FCSTD DOCUMENT  (FreeCAD 0.18.4R)
Label: container.v5
License: All rights reserved
LicenseURL: http://en.wikipedia.org/wiki/All_rights_reserved
objects: Part::Extrusion×24, Part::Feature×12, Part::Part2DObjectPython×12, Part::Cut×11, Part::MultiFuse×11
note: 70 computed .brp shape members not serialized (recipe doc carries the construction recipe); baked Part::Feature solids carry a one-line shape summary decoded from their .brp

FEATURE [Part::Feature] Cut001001  label="Cut002"
  shape: bbox 73.48 x 120 x 121.6 mm, 4537 faces (baked)
FEATURE [Part::Feature] Fusion018002001008015
  shape: bbox 73.48 x 120 x 121.6 mm, 4525 faces (baked)
FEATURE [Part::Feature] Fusion018002001008014
  Placement = pos=(1.059e-12,-240,-121.554) rot=(0,0,1;0rad)
  shape: bbox 46.3 x 120 x 5.151 mm, 1154 faces (baked)
FEATURE [Part::Part2DObjectPython] Rectangle  # Draft 2D object (typed FeaturePython)
  ChamferSize = 0
  Columns = 1
  FilletRadius = 0
  Height = 120
  Length = 112.55
  MakeFace = true
  Placement = pos=(139.139,-112.777,-9.82831) rot=(0,1,0;1.46952rad)
  Rows = 1
FEATURE [Part::Extrusion] Extrusion
  Base = -> Rectangle
  Dir = (9.01598,-9e-16,0.916258)
  DirMode = 0
  FaceMakerClass = Part::FaceMakerBullseye
  LengthFwd = 0
  LengthRev = 0
  Solid = true
  Symmetric = false
FEATURE [Part::Cut] Cut
  Base = -> Fusion018002001008015
  Tool = -> Extrusion
FEATURE [Part::Feature] Face001
  Placement = pos=(20.8688,3.98e-13,-59.6902) rot=(0,0,1;0rad)
  shape: bbox 0.5074 x 117 x 4.974 mm, 1 faces, 0 solids (baked)
FEATURE [Part::Extrusion] Extrusion002
  Base = -> Face001
  Dir = (1.9794,3.87e-14,0.201929)
  DirMode = 0
  FaceMakerClass = Part::FaceMakerBullseye
  LengthFwd = 0
  LengthRev = 0
  Solid = true
  Symmetric = false
FEATURE [Part::Part2DObjectPython] Wire001  # Draft 2D object (typed FeaturePython)
  ChamferSize = 0
  Closed = true
  End = (150.569,7.2227,-121.796)
  FilletRadius = 0
  Length = 3.03695
  MakeFace = true
  Placement = pos=(150.519,7.2227,-121.802) rot=(-1,0,0;1.5708rad)
  Points = (3) [(0,0,0),(0.207003,1.47911,-5.72875e-13),(0.0507037,-0.00515282,-2.84217e-14)]
  Start = (150.519,7.2227,-121.802)
  Subdivisions = 0
FEATURE [Part::Extrusion] Extrusion001
  Base = -> Wire001
  Dir = (-6.89207e-11,-133.783,4.03232e-11)
  DirMode = 0
  FaceMakerClass = Part::FaceMakerBullseye
  LengthFwd = 0
  LengthRev = 0
  Solid = true
  Symmetric = false
FEATURE [Part::Cut] Cut001
  Base = -> Cut
  Tool = -> Extrusion001
FEATURE [Part::Part2DObjectPython] Rectangle001  # Draft 2D object (typed FeaturePython)
  ChamferSize = 0
  Columns = 1
  FilletRadius = 0
  Height = 18.318
  Length = 268.185
  MakeFace = true
  Placement = pos=(134.572,-92.7773,-10.1413) rot=(0.742121,0,-0.670265;3.14159rad)
  Rows = 1
FEATURE [Part::Extrusion] Extrusion004
  Base = -> Rectangle001
  Dir = (3.0678,6.99e-14,0.312963)
  DirMode = 0
  FaceMakerClass = Part::FaceMakerBullseye
  LengthFwd = 0
  LengthRev = 0
  Solid = true
  Symmetric = false
FEATURE [Part::MultiFuse] Fusion
  Shapes = -> [Extrusion002,Cut001001]
FEATURE [Part::Cut] Cut001002
  Base = -> Fusion
  Tool = -> Extrusion004
FEATURE [Part::Part2DObjectPython] Rectangle002  # Draft 2D object (typed FeaturePython)
  ChamferSize = 0
  Columns = 1
  FilletRadius = 0
  Height = 18.682
  Length = 300.185
  MakeFace = true
  Placement = pos=(134.572,5.9047,-10.1413) rot=(0.742121,0,-0.670265;3.14159rad)
  Rows = 1
FEATURE [Part::Extrusion] Extrusion005
  Base = -> Rectangle002
  Dir = (3.0678,6.99e-14,0.312963)
  DirMode = 0
  FaceMakerClass = Part::FaceMakerBullseye
  LengthFwd = 0
  LengthRev = 0
  Solid = true
  Symmetric = false
FEATURE [Part::Cut] Cut001003
  Base = -> Cut001002
  Tool = -> Extrusion005
FEATURE [Part::Part2DObjectPython] Rectangle003  # Draft 2D object (typed FeaturePython)
  ChamferSize = 0
  Columns = 1
  FilletRadius = 0
  Height = 3
  Length = 5
  MakeFace = true
  Placement = pos=(137.077,-9.7773,-34.6992) rot=(0.742121,0,-0.670265;3.14159rad)
  Rows = 1
FEATURE [Part::Extrusion] Extrusion006
  Base = -> Rectangle003
  Dir = (4.54052,1.035e-13,0.463202)
  DirMode = 0
  FaceMakerClass = Part::FaceMakerBullseye
  LengthFwd = 0
  LengthRev = 0
  Placement = pos=(1.251e-12,-73,7.46e-13) rot=(0,0,1;0rad)
  Solid = true
  Symmetric = false
FEATURE [Part::Extrusion] Extrusion007
  Base = -> Rectangle003
  Dir = (4.54052,1.035e-13,0.463202)
  DirMode = 0
  FaceMakerClass = Part::FaceMakerBullseye
  LengthFwd = 0
  LengthRev = 0
  Placement = pos=(2.27e-13,-10,5.7e-14) rot=(0,0,1;0rad)
  Solid = true
  Symmetric = false
FEATURE [Part::Extrusion] Extrusion008
  Base = -> Rectangle003
  Dir = (4.54052,1.035e-13,0.463202)
  DirMode = 0
  FaceMakerClass = Part::FaceMakerBullseye
  LengthFwd = 0
  LengthRev = 0
  Placement = pos=(6.31104,-83,-61.8636) rot=(0,0,1;0rad)
  Solid = true
  Symmetric = false
FEATURE [Part::Extrusion] Extrusion009
  Base = -> Rectangle003
  Dir = (4.54052,1.035e-13,0.463202)
  DirMode = 0
  FaceMakerClass = Part::FaceMakerBullseye
  LengthFwd = 0
  LengthRev = 0
  Placement = pos=(6.31104,-2.132e-13,-61.8636) rot=(0,0,1;0rad)
  Solid = true
  Symmetric = false
FEATURE [Part::Feature] Face
  Placement = pos=(147.928,-92.7773,-96.0997) rot=(0.742121,0,-0.670265;3.14159rad)
  shape: bbox 0.5074 x 3 x 4.974 mm, 1 faces, 0 solids (baked)
FEATURE [Part::Extrusion] Extrusion010
  Base = -> Face
  Dir = (-0.0226524,-5e-16,-0.0023109)
  DirMode = 0
  FaceMakerClass = Part::FaceMakerBullseye
  LengthFwd = 0
  LengthRev = 0
  Solid = true
  Symmetric = false
FEATURE [Part::Cut] Cut001004
  Base = -> Extrusion008
  Placement = pos=(-2.27e-13,10,-8.5e-14) rot=(0,0,1;0rad)
  Tool = -> Extrusion010
FEATURE [Part::Feature] Face003
  Placement = pos=(147.928,-9.7773,-96.0997) rot=(0.742121,0,-0.670265;3.14159rad)
  shape: bbox 0.5074 x 3 x 4.974 mm, 1 faces, 0 solids (baked)
FEATURE [Part::Extrusion] Extrusion011
  Base = -> Face003
  Dir = (-0.0226524,-5e-16,-0.0023109)
  DirMode = 0
  FaceMakerClass = Part::FaceMakerBullseye
  LengthFwd = 0
  LengthRev = 0
  Solid = true
  Symmetric = false
FEATURE [Part::Cut] Cut001005
  Base = -> Extrusion009
  Placement = pos=(3.13e-13,-10,8.5e-14) rot=(0,0,1;0rad)
  Tool = -> Extrusion011
FEATURE [Part::Feature] Face004
  shape: bbox 2.487 x 3e-07 x 5.176 mm, 1 faces, 0 solids (baked)
FEATURE [Part::Extrusion] Extrusion012
  Base = -> Face004
  Dir = (2.218e-13,-10,6e-14)
  DirMode = 0
  FaceMakerClass = Part::FaceMakerBullseye
  LengthFwd = 0
  LengthRev = 0
  Solid = true
  Symmetric = false
FEATURE [Part::Feature] Face005
  shape: bbox 2.507 x 3e-07 x 4.974 mm, 1 faces, 0 solids (baked)
FEATURE [Part::Extrusion] Extrusion013
  Base = -> Face005
  Dir = (2.218e-13,-10,6e-14)
  DirMode = 0
  FaceMakerClass = Part::FaceMakerBullseye
  LengthFwd = 0
  LengthRev = 0
  Solid = true
  Symmetric = false
FEATURE [Part::Cut] Cut001006
  Base = -> Cut001003
  Tool = -> Extrusion013
FEATURE [Part::Cut] Cut001007
  Base = -> Cut001006
  Tool = -> Extrusion012
FEATURE [Part::Feature] Face006
  shape: bbox 2.487 x 3e-07 x 5.176 mm, 1 faces, 0 solids (baked)
FEATURE [Part::Extrusion] Extrusion014
  Base = -> Face006
  Dir = (-2.218e-13,10,-6e-14)
  DirMode = 0
  FaceMakerClass = Part::FaceMakerBullseye
  LengthFwd = 0
  LengthRev = 0
  Solid = true
  Symmetric = false
FEATURE [Part::Feature] Face007
  shape: bbox 2.507 x 3e-07 x 4.974 mm, 1 faces, 0 solids (baked)
FEATURE [Part::Extrusion] Extrusion015
  Base = -> Face007
  Dir = (-2.218e-13,10,-6e-14)
  DirMode = 0
  FaceMakerClass = Part::FaceMakerBullseye
  LengthFwd = 0
  LengthRev = 0
  Solid = true
  Symmetric = false
FEATURE [Part::Cut] Cut001008
  Base = -> Cut001007
  Tool = -> Extrusion014
FEATURE [Part::Cut] Cut001009
  Base = -> Cut001008
  Tool = -> Extrusion015
FEATURE [Part::Part2DObjectPython] Wire  # Draft 2D object (typed FeaturePython)
  ChamferSize = 0
  Closed = true
  End = (147.232,-19.7773,-104.212)
  FilletRadius = 0
  Length = 10.3246
  MakeFace = true
  Placement = pos=(146.928,-19.7773,-101.228) rot=(-0.12867,0.965149,0.227886;3.51829rad)
  Points = (3) [(0,0,0),(2.63038,0.326583,1.50475),(-1.1641,-1.45553,2.35081)]
  Start = (146.928,-19.7773,-101.228)
  Subdivisions = 0
FEATURE [Part::Extrusion] Extrusion016
  Base = -> Wire
  Dir = (4.73e-14,-3,2.76e-14)
  DirMode = 0
  FaceMakerClass = Part::FaceMakerBullseye
  LengthFwd = 0
  LengthRev = 0
  Solid = true
  Symmetric = false
FEATURE [Part::Extrusion] Extrusion018
  Base = -> Wire
  Dir = (4.73e-14,-3,2.76e-14)
  DirMode = 0
  FaceMakerClass = Part::FaceMakerBullseye
  LengthFwd = 0
  LengthRev = 0
  Placement = pos=(1.336e-12,-63,6.25e-13) rot=(0,0,1;0rad)
  Solid = true
  Symmetric = false
FEATURE [Part::Part2DObjectPython] Wire002  # Draft 2D object (typed FeaturePython)
  ChamferSize = 0
  Closed = true
  End = (143.895,-82.7773,-101.537)
  FilletRadius = 0
  Length = 6.54559
  MakeFace = true
  Placement = pos=(146.073,-82.7773,-103.283) rot=(-1,0,0;1.5708rad)
  Points = (3) [(0,0,0),(-0.177414,-1.74576,2.84217e-14),(-2.17741,-1.74576,7.10543e-14)]
  Start = (146.073,-82.7773,-103.283)
  Subdivisions = 0
  Support = -> [Extrusion018]
FEATURE [Part::Extrusion] Extrusion019
  Base = -> Wire002
  Dir = (-5.008e-13,60,-1.5064e-12)
  DirMode = 0
  FaceMakerClass = Part::FaceMakerBullseye
  LengthFwd = 0
  LengthRev = 0
  Solid = true
  Symmetric = false
FEATURE [Part::MultiFuse] Fusion018002001008016
  Shapes = -> [Extrusion016,Extrusion019,Extrusion018]
FEATURE [Part::MultiFuse] Fusion018002001008017
  Placement = pos=(-6.31104,5.258e-13,61.8636) rot=(0,0,1;0rad)
  Shapes = -> [Extrusion016,Extrusion019,Extrusion018]
FEATURE [Part::MultiFuse] Fusion018002001008018
  Shapes = -> [Fusion018002001008017,Cut001009]
FEATURE [Part::MultiFuse] Fusion018002001008019
  Shapes = -> [Fusion018002001008016,Fusion018002001008018]
FEATURE [Part::MultiFuse] Fusion018002001008020
  Shapes = -> [Extrusion007,Extrusion006,Cut001004,Cut001005,Fusion018002001008019]
FEATURE [Part::Part2DObjectPython] Wire003  # Draft 2D object (typed FeaturePython)
  ChamferSize = 0
  Closed = true
  End = (148.381,-19.6273,-100.761)
  FilletRadius = 0
  Length = 7.79808
  MakeFace = true
  Placement = pos=(148.52,-18.2487,-102.133) rot=(0,1,0;1.46952rad)
  Points = (4) [(0,0,0),(1.37849,-1.3786,0),(-0.000105983,-2.75709,0),(-1.37849,-1.3786,-8.52651e-14)]
  Start = (148.52,-18.2487,-102.133)
  Subdivisions = 0
FEATURE [Part::Extrusion] Extrusion020
  Base = -> Wire003
  Dir = (-1.48467,1e-16,-0.150881)
  DirMode = 0
  FaceMakerClass = Part::FaceMakerBullseye
  LengthFwd = 0
  LengthRev = 0
  Solid = true
  Symmetric = false
FEATURE [Part::MultiFuse] Fusion018002001008021
  Shapes = -> [Fusion018002001008020,Extrusion020]
FEATURE [Part::Part2DObjectPython] Wire004  # Draft 2D object (typed FeaturePython)
  ChamferSize = 0
  Closed = true
  End = (141.767,-87.5055,-35.6858)
  FilletRadius = 0
  Length = 17.6963
  MakeFace = true
  Placement = pos=(141.628,-86.1273,-34.3147) rot=(0,1,0;1.46952rad)
  Points = (4) [(0,0,0),(4.8786,4.87822,0),(6.25672,3.5,0),(1.37812,-1.37822,0)]
  Start = (141.628,-86.1273,-34.3147)
  Subdivisions = 0
FEATURE [Part::Extrusion] Extrusion021
  Base = -> Wire004
  Dir = (-1.48467,-9.8e-15,-0.150881)
  DirMode = 0
  FaceMakerClass = Part::FaceMakerBullseye
  LengthFwd = 0
  LengthRev = 0
  Solid = true
  Symmetric = false
FEATURE [Part::MultiFuse] Fusion018002001008022
  Shapes = -> [Fusion018002001008021,Extrusion021]
FEATURE [Part::Part2DObjectPython] Wire005  # Draft 2D object (typed FeaturePython)
  ChamferSize = 0
  Closed = true
  End = (141.628,-23.1273,-34.3147)
  FilletRadius = 0
  Length = 17.6973
  MakeFace = true
  Placement = pos=(142.121,-18.2487,-39.168) rot=(0,1,0;1.46952rad)
  Points = (4) [(0,0,0),(1.37849,-1.3786,-2.84217e-14),(-3.49973,-6.2572,-2.84217e-14),(-4.87822,-4.8786,-1.42109e-13)]
  Start = (142.121,-18.2487,-39.168)
  Subdivisions = 0
FEATURE [Part::Extrusion] Extrusion022
  Base = -> Wire005
  Dir = (-1.48467,4.5e-15,-0.150881)
  DirMode = 0
  FaceMakerClass = Part::FaceMakerBullseye
  LengthFwd = 0
  LengthRev = 0
  Solid = true
  Symmetric = false
FEATURE [Part::MultiFuse] Fusion018002001008023
  Shapes = -> [Extrusion022,Fusion018002001008022]
FEATURE [Part::Part2DObjectPython] Wire006  # Draft 2D object (typed FeaturePython)
  ChamferSize = 0
  Closed = true
  End = (148.659,-82.6273,-103.504)
  FilletRadius = 0
  Length = 24.6968
  MakeFace = true
  Placement = pos=(148.52,-81.2487,-102.133) rot=(0,1,0;1.46952rad)
  Points = (5) [(0,0,0),(-6.99946,-5.68434e-14,-1.98952e-13),(-8.37795,-1.3786,-3.97904e-13),(-3.49973,-6.2572,0),(1.37849,-1.3786,2.84217e-14)]
  Start = (148.52,-81.2487,-102.133)
  Subdivisions = 0
FEATURE [Part::Extrusion] Extrusion023
  Base = -> Wire006
  Dir = (-1.48467,-3.21e-14,-0.150881)
  DirMode = 0
  FaceMakerClass = Part::FaceMakerBullseye
  LengthFwd = 0
  LengthRev = 0
  Solid = true
  Symmetric = false
FEATURE [Part::MultiFuse] Fusion018002001008024
  Shapes = -> [Extrusion023,Fusion018002001008023]
FEATURE [Part::Part2DObjectPython] Wire007  # Draft 2D object (typed FeaturePython)
  ChamferSize = 0
  Closed = true
  End = (147.673,-19.6273,-93.7977)
  FilletRadius = 0
  Length = 17.6973
  MakeFace = true
  Placement = pos=(147.812,-18.2487,-95.1691) rot=(-0.522981,0.449209,-0.724363;1.96689rad)
  Points = (4) [(0,0,0),(4.30866,5.21713,-1.34714),(5.83135,4.03562,-1.05347),(1.52268,-1.18151,0.293667)]
  Start = (147.812,-18.2487,-95.1691)
  Subdivisions = 0
FEATURE [Part::Extrusion] Extrusion024
  Base = -> Wire007
  Dir = (-1.48467,1.35e-14,-0.150881)
  DirMode = 0
  FaceMakerClass = Part::FaceMakerBullseye
  LengthFwd = 0
  LengthRev = 0
  Solid = true
  Symmetric = false
FEATURE [Part::MultiFuse] Fusion018002001008025
  Shapes = -> [Fusion018002001008024,Extrusion024]
FEATURE [Part::Feature] Fusion018002001008025001  label="Fusion018002001008026"
  shape: bbox 73.48 x 120 x 121.6 mm, 4578 faces (baked)
FEATURE [Part::Feature] Face008
  shape: bbox 0.09973 x 1.08e-06 x 0.9776 mm, 1 faces, 0 solids (baked)
FEATURE [Part::Extrusion] Extrusion025
  Base = -> Face008
  Dir = (1.7744e-12,-80,4.8e-13)
  DirMode = 0
  FaceMakerClass = Part::FaceMakerBullseye
  LengthFwd = 0
  LengthRev = 0
  Solid = true
  Symmetric = false
FEATURE [Part::Cut] Cut001010
  Base = -> Fusion018002001008025001
  Tool = -> Extrusion025
